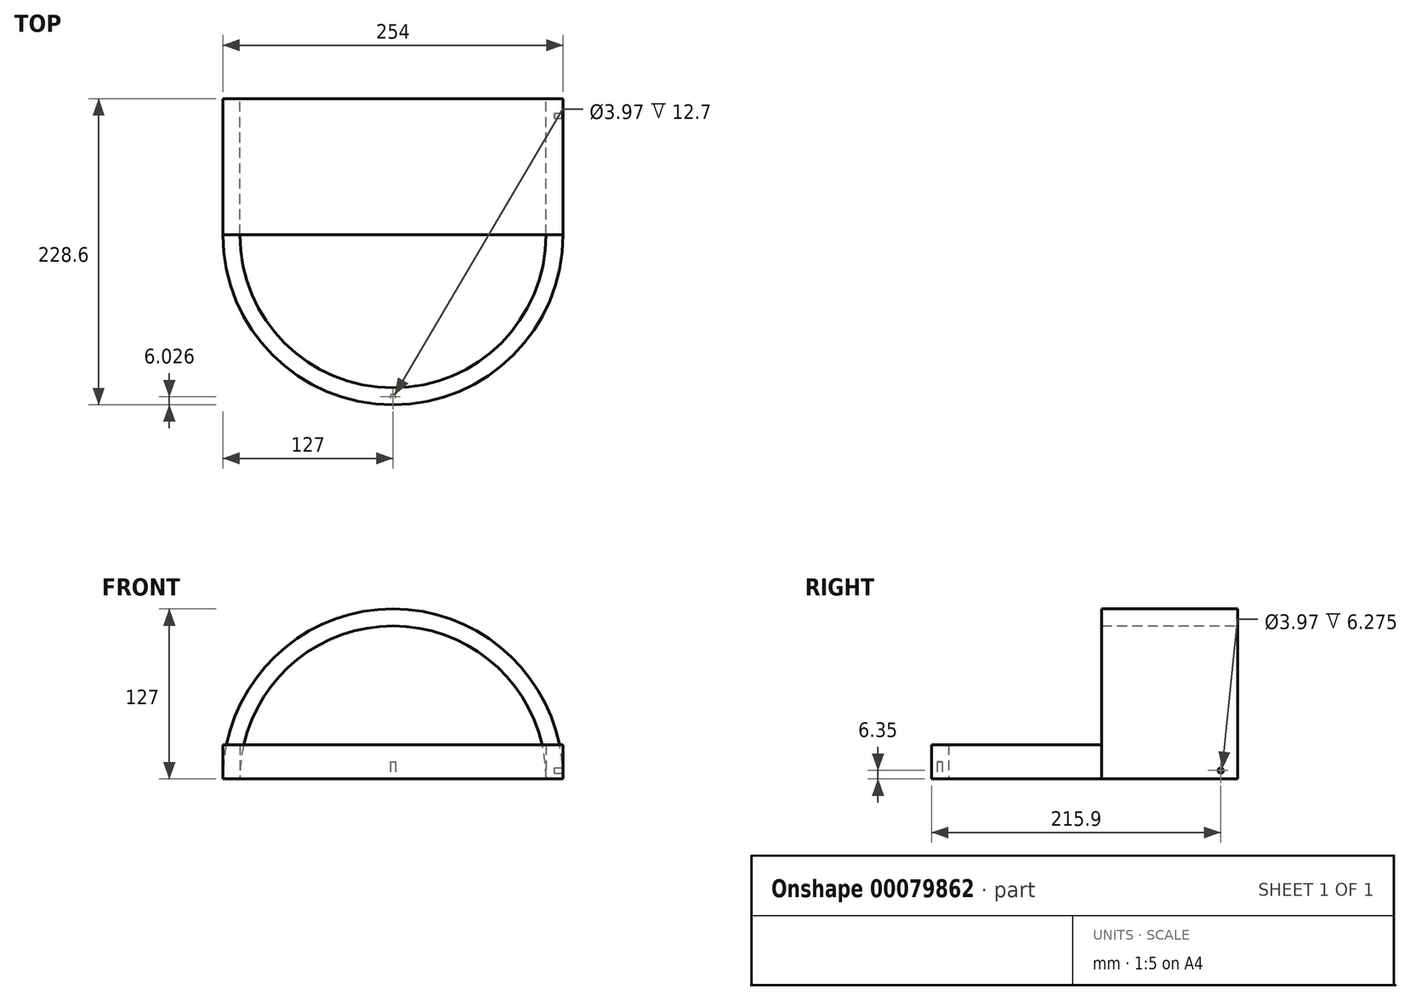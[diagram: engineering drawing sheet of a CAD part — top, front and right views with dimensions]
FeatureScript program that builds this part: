
annotation { "Feature Type Name" : "Feature", "Feature Type Description" : "" }
export const myFeature = defineFeature(function(context is Context, id is Id, definition is map)
    precondition{}
    {
        {
            var Q0;
            Q0=qCreatedBy(makeId("Front.planeOp"),FACE);
            var sketch = newSketch(context, id + "F0", { "sketchPlane" : qUnion([Q0])});
            skArc(sketch, "E0", {"start": v(127, 0) * mm, "mid": v(0, 127) * mm, "end": v(-127, 0) * mm});
            skArc(sketch, "E1", {"start": v(114.3, 0) * mm, "mid": v(0, 114.3) * mm, "end": v(-114.3, 0) * mm});
            skLineSegment(sketch, "E2", {"start": v(-127, 0) * mm, "end": v(-114.3, 0) * mm});
            skPoint(sketch, "E3.orphan", {"position": v(-175.8, 0) * mm});
            skLineSegment(sketch, "E4.trimOffspring", {"start": v(114.3, 0) * mm, "end": v(127, 0) * mm});
            skSolve(sketch);
        }
        {
            var Q0;
            Q0=makeQuery(id+"F0.imprint","IMPRINT",FACE,{"disambiguationData":[TD([[makeQuery(id+"F0.imprint","IMPRINT",EDGE,{"derivedFrom":sQuery(id+"F0.wireOp",EDGE,"E0")}),1.0]])]});
            extrude(context, id + "F1", {"entities" : qUnion([Q0]), "depth" : 101.6 * mm});
        }
        {
            var Q0;
            Q0=makeQuery(id+"F1.opExtrude","SWEPT_FACE",FACE,{"disambiguationData":[OSD([sQuery(id+"F0.wireOp",EDGE,"E2")])]});
            var sketch = newSketch(context, id + "F2", { "sketchPlane" : qUnion([Q0])});
            skPoint(sketch, "E5.0", {"position": v(-114.3, 101.6) * mm});
            skPoint(sketch, "E6.0", {"position": v(-127, 101.6) * mm});
            skPoint(sketch, "E7.0", {"position": v(114.3, 101.6) * mm});
            skPoint(sketch, "E8.0", {"position": v(127, 101.6) * mm});
            skArc(sketch, "E9", {"start": v(114.3, 101.6) * mm, "mid": v(0, 215.9) * mm, "end": v(-114.3, 101.6) * mm});
            skArc(sketch, "E10", {"start": v(127, 101.6) * mm, "mid": v(0, 228.6) * mm, "end": v(-127, 101.6) * mm});
            skLineSegment(sketch, "E11", {"start": v(-127, 101.6) * mm, "end": v(-114.3, 101.6) * mm});
            skLineSegment(sketch, "E12", {"start": v(114.3, 101.6) * mm, "end": v(127, 101.6) * mm});
            skSolve(sketch);
        }
        {
            var Q0;
            Q0=makeQuery(id+"FRI2kO9llWMQubz_1.boolean.opBoolean","MERGE",FACE,{"derivedFrom":[makeQuery(id+"F1.opExtrude","SWEPT_FACE",FACE,{"disambiguationData":[OSD([sQuery(id+"F0.wireOp",EDGE,"E2")])]}),makeQuery(id+"F1.opExtrude","SWEPT_FACE",FACE,{"disambiguationData":[OSD([sQuery(id+"F0.wireOp",EDGE,"E4.trimOffspring")])]}),makeQuery(id+"FRI2kO9llWMQubz_1.opRevolve","CAP_FACE",FACE,{"disambiguationData":[OSD([sQuery(id+"F2.wireOp",EDGE,"E9"),sQuery(id+"F2.wireOp",EDGE,"E10"),sQuery(id+"F2.wireOp",EDGE,"E11"),sQuery(id+"F2.wireOp",EDGE,"E12")])],"isStart":true})]});
            var sketch = newSketch(context, id + "F3", { "sketchPlane" : qUnion([Q0])});
            skCircle(sketch, "E13", {"center": v(0, 222.57) * mm, "radius": 1.98 * mm});
            skSolve(sketch);
        }
        {
            var Q0;
            Q0=makeQuery(id+"F3.imprint","IMPRINT",FACE,{"disambiguationData":[TD([[makeQuery(id+"F3.imprint","IMPRINT",EDGE,{"derivedFrom":sQuery(id+"F3.wireOp",EDGE,"E13")}),1.0]])]});
            extrude(context, id + "F4", {"entities" : qUnion([Q0]), "operationType" : NewBodyOperationType.REMOVE, "oppositeDirection" : true, "depth" : 25.4 * mm});
        }
        {
            var Q0;
            Q0=qCreatedBy(makeId("Right.planeOp"),FACE);
            cPlane(context, id + "F5", {"entities" : qUnion([Q0]), "cplaneType" : CPlaneType.OFFSET, "offset" : 152.4 * mm, "width" : 152.4 * mm, "height" : 152.4 * mm});
        }
        {
            var Q0;
            Q0=qCreatedBy(id+"F5.planeOp",FACE);
            var sketch = newSketch(context, id + "F6", { "sketchPlane" : qUnion([Q0])});
            skCircle(sketch, "E14", {"center": v(-12.7, 6.35) * mm, "radius": 1.98 * mm});
            skLineSegment(sketch, "E15.0", {"start": v(-101.6, 0) * mm, "end": v(0, 0) * mm});
            skSolve(sketch);
        }
        {
            var Q0;
            Q0=makeQuery(id+"F6.imprint","IMPRINT",FACE,{"disambiguationData":[TD([[makeQuery(id+"F6.imprint","IMPRINT",EDGE,{"derivedFrom":sQuery(id+"F6.wireOp",EDGE,"E14")}),1.0]])]});
            extrude(context, id + "F7", {"entities" : qUnion([Q0]), "operationType" : NewBodyOperationType.REMOVE, "oppositeDirection" : true, "depth" : 31.75 * mm});
        }
        {
            var Q0;
            Q0=makeQuery(id+"F2.imprint","IMPRINT",FACE,{"disambiguationData":[TD([[makeQuery(id+"F2.imprint","IMPRINT",EDGE,{"derivedFrom":sQuery(id+"F2.wireOp",EDGE,"E9")}),-1.0]])]});
            extrude(context, id + "F8", {"entities" : qUnion([Q0]), "operationType" : NewBodyOperationType.ADD, "oppositeDirection" : true, "depth" : 25.4 * mm});
        }
        {
            var Q0;
            Q0=makeQuery(id+"F3.imprint","IMPRINT",FACE,{"disambiguationData":[TD([[makeQuery(id+"F3.imprint","IMPRINT",EDGE,{"derivedFrom":sQuery(id+"F3.wireOp",EDGE,"E13")}),1.0]])]});
            extrude(context, id + "F9", {"entities" : qUnion([Q0]), "operationType" : NewBodyOperationType.REMOVE, "oppositeDirection" : true, "depth" : 12.7 * mm});
        }
    });
